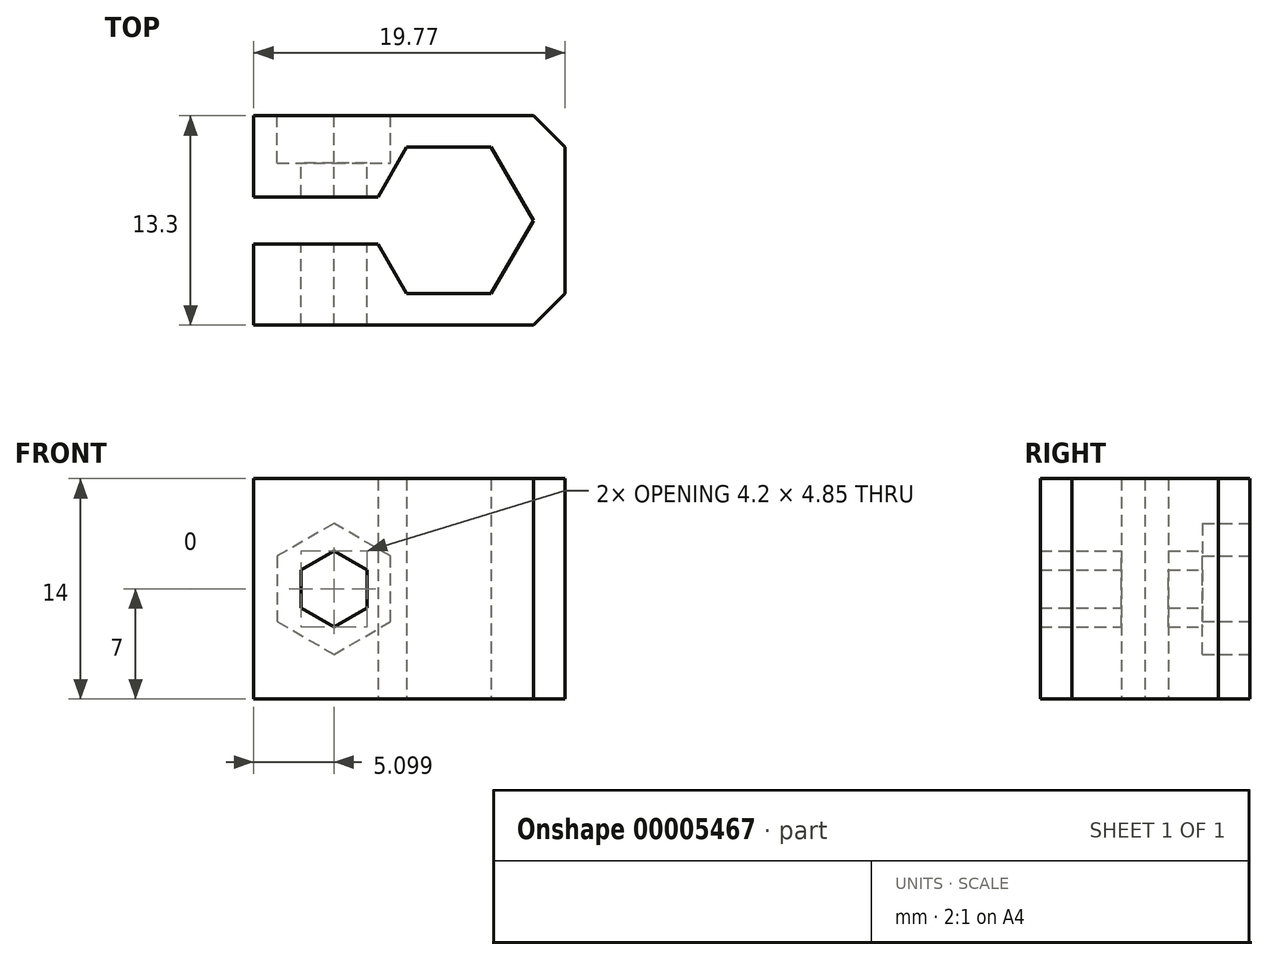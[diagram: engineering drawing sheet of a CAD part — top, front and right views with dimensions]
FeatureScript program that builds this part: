
annotation { "Feature Type Name" : "Feature", "Feature Type Description" : "" }
export const myFeature = defineFeature(function(context is Context, id is Id, definition is map)
    precondition{}
    {
        {
            var Q0;
            Q0=qCreatedBy(makeId("Top.planeOp"),FACE);
            var sketch = newSketch(context, id + "F0", { "sketchPlane" : qUnion([Q0])});
            skArc(sketch, "E0", {"start": v(-4.4, -1.5) * mm, "mid": v(4.65, 0) * mm, "end": v(-4.4, 1.5) * mm, "construction": true});
            skLineSegment(sketch, "E1", {"start": v(-4.4, 1.5) * mm, "end": v(-12.4, 1.5) * mm});
            skLineSegment(sketch, "E2", {"start": v(-12.4, 1.5) * mm, "end": v(-12.4, 6.65) * mm});
            skLineSegment(sketch, "E3", {"start": v(-12.4, 6.65) * mm, "end": v(7.37, 6.65) * mm});
            skLineSegment(sketch, "E4", {"start": v(7.37, 6.65) * mm, "end": v(7.37, -6.65) * mm});
            skLineSegment(sketch, "E5", {"start": v(7.37, -6.65) * mm, "end": v(-12.4, -6.65) * mm});
            skLineSegment(sketch, "E6", {"start": v(-12.4, -6.65) * mm, "end": v(-12.4, -1.5) * mm});
            skLineSegment(sketch, "E7", {"start": v(-12.4, -1.5) * mm, "end": v(-4.4, -1.5) * mm});
            skCircle(sketch, "E8.cCircle", {"center": v(0, 0) * mm, "radius": 4.65 * mm, "construction": true});
            skLineSegment(sketch, "E8.0", {"start": v(-2.68, -4.65) * mm, "end": v(-5.37, 0) * mm});
            skLineSegment(sketch, "E8.1", {"start": v(-5.37, 0) * mm, "end": v(-2.68, 4.65) * mm});
            skLineSegment(sketch, "E8.2", {"start": v(-2.68, 4.65) * mm, "end": v(2.68, 4.65) * mm});
            skLineSegment(sketch, "E8.3", {"start": v(2.68, 4.65) * mm, "end": v(5.37, 0) * mm});
            skLineSegment(sketch, "E8.4", {"start": v(5.37, 0) * mm, "end": v(2.68, -4.65) * mm});
            skLineSegment(sketch, "E8.5", {"start": v(2.68, -4.65) * mm, "end": v(-2.68, -4.65) * mm});
            skPoint(sketch, "E8.0.midPoint", {"position": v(-4.03, -2.32) * mm});
            skSolve(sketch);
        }
        {
            var Q0;
            Q0=makeQuery(id+"F0.imprint","IMPRINT",FACE,{"disambiguationData":[TD([[makeQuery(id+"F0.imprint","IMPRINT",EDGE,{"derivedFrom":sQuery(id+"F0.wireOp",EDGE,"E0")}),-1.0]])]});
            var Q1;
            {var subQ9=sQuery(id+"F0.wireOp",EDGE,"E2");Q1=makeQuery(id+"F0.imprint","IMPRINT",FACE,{"disambiguationData":[TD([[makeQuery(id+"F0.imprint","IMPRINT",EDGE,{"derivedFrom":subQ9}),-1.0]])]});}
            extrude(context, id + "F1", {"entities" : qUnion([Q0, Q1]), "depth" : 14 * mm});
        }
        {
            var Q0;
            Q0=makeQuery(id+"F1.opExtrude","SWEPT_FACE",FACE,{"disambiguationData":[OSD([sQuery(id+"F0.wireOp",EDGE,"E3")])]});
            var sketch = newSketch(context, id + "F2", { "sketchPlane" : qUnion([Q0])});
            skCircle(sketch, "E9.cCircle", {"center": v(7.3, 7) * mm, "radius": 3.6 * mm, "construction": true});
            skLineSegment(sketch, "E9.0", {"start": v(3.7, 4.92) * mm, "end": v(3.7, 9.08) * mm});
            skLineSegment(sketch, "E9.1", {"start": v(3.7, 9.08) * mm, "end": v(7.3, 11.16) * mm});
            skLineSegment(sketch, "E9.2", {"start": v(7.3, 11.16) * mm, "end": v(10.9, 9.08) * mm});
            skLineSegment(sketch, "E9.3", {"start": v(10.9, 9.08) * mm, "end": v(10.9, 4.92) * mm});
            skLineSegment(sketch, "E9.4", {"start": v(10.9, 4.92) * mm, "end": v(7.3, 2.84) * mm});
            skLineSegment(sketch, "E9.5", {"start": v(7.3, 2.84) * mm, "end": v(3.7, 4.92) * mm});
            skPoint(sketch, "E9.0.midPoint", {"position": v(3.7, 7) * mm});
            skCircle(sketch, "E10.cCircle", {"center": v(7.3, 7) * mm, "radius": 2.1 * mm, "construction": true});
            skLineSegment(sketch, "E10.0", {"start": v(5.2, 5.79) * mm, "end": v(5.2, 8.21) * mm});
            skLineSegment(sketch, "E10.1", {"start": v(5.2, 8.21) * mm, "end": v(7.3, 9.42) * mm});
            skLineSegment(sketch, "E10.2", {"start": v(7.3, 9.42) * mm, "end": v(9.4, 8.21) * mm});
            skLineSegment(sketch, "E10.3", {"start": v(9.4, 8.21) * mm, "end": v(9.4, 5.79) * mm});
            skLineSegment(sketch, "E10.4", {"start": v(9.4, 5.79) * mm, "end": v(7.3, 4.58) * mm});
            skLineSegment(sketch, "E10.5", {"start": v(7.3, 4.58) * mm, "end": v(5.2, 5.79) * mm});
            skPoint(sketch, "E10.0.midPoint", {"position": v(5.2, 7) * mm});
            skPoint(sketch, "E11", {"position": v(12.4, 7) * mm});
            skSolve(sketch);
        }
        {
            var Q0;
            Q0=makeQuery(id+"F2.imprint","IMPRINT",FACE,{"disambiguationData":[TD([[makeQuery(id+"F2.imprint","IMPRINT",EDGE,{"derivedFrom":sQuery(id+"F2.wireOp",EDGE,"E10.0")}),-1.0]])]});
            extrude(context, id + "F3", {"entities" : qUnion([Q0]), "operationType" : NewBodyOperationType.REMOVE, "endBound" : BoundingType.THROUGH_ALL, "oppositeDirection" : true, "depth" : 25 * mm});
        }
        {
            var Q0;
            Q0=makeQuery(id+"F2.imprint","IMPRINT",FACE,{"disambiguationData":[TD([[makeQuery(id+"F2.imprint","IMPRINT",EDGE,{"derivedFrom":sQuery(id+"F2.wireOp",EDGE,"E9.0")}),-1.0]])]});
            extrude(context, id + "F4", {"entities" : qUnion([Q0]), "operationType" : NewBodyOperationType.REMOVE, "oppositeDirection" : true, "depth" : 3 * mm});
        }
        {
            var Q0;
            Q0=makeQuery(id+"F1.opExtrude","SWEPT_EDGE",EDGE,{"disambiguationData":[OSD([sQuery(id+"F0.wireOp",EDGE,"E3"),sQuery(id+"F0.wireOp",EDGE,"E4")])]});
            var Q1;
            Q1=makeQuery(id+"F1.opExtrude","SWEPT_EDGE",EDGE,{"disambiguationData":[OSD([sQuery(id+"F0.wireOp",EDGE,"E4"),sQuery(id+"F0.wireOp",EDGE,"E5")])]});
            chamfer(context, id + "F5", {"entities" : qUnion([Q0, Q1]), "width" : 2 * mm, "tangentPropagation" : true});
        }
        {
            var Q0;
            Q0=makeQuery(id+"F4.boolean.opBoolean","COPY",FACE,{"derivedFrom":makeQuery(id+"F4.opExtrude","CAP_FACE",FACE,{"disambiguationData":[OSD([sQuery(id+"F2.wireOp",EDGE,"E9.0"),sQuery(id+"F2.wireOp",EDGE,"E9.1"),sQuery(id+"F2.wireOp",EDGE,"E9.2"),sQuery(id+"F2.wireOp",EDGE,"E9.3"),sQuery(id+"F2.wireOp",EDGE,"E9.4"),sQuery(id+"F2.wireOp",EDGE,"E9.5"),sQuery(id+"F2.wireOp",EDGE,"E10.0"),sQuery(id+"F2.wireOp",EDGE,"E10.1"),sQuery(id+"F2.wireOp",EDGE,"E10.2"),sQuery(id+"F2.wireOp",EDGE,"E10.3"),sQuery(id+"F2.wireOp",EDGE,"E10.4"),sQuery(id+"F2.wireOp",EDGE,"E10.5")])],"isStart":false})});
            var sketch = newSketch(context, id + "F6", { "sketchPlane" : qUnion([Q0])});
            skPoint(sketch, "E12.0", {"position": v(7.3, 7) * mm});
            skSolve(sketch);
        }
        {
            var Q0;
            Q0=makeQuery(id+"F1.opExtrude","SWEPT_FACE",FACE,{"disambiguationData":[OSD([sQuery(id+"F0.wireOp",EDGE,"E5")])]});
            var sketch = newSketch(context, id + "F7", { "sketchPlane" : qUnion([Q0])});
            skPoint(sketch, "E13.0", {"position": v(-7.3, 7) * mm});
            skSolve(sketch);
        }
    });
